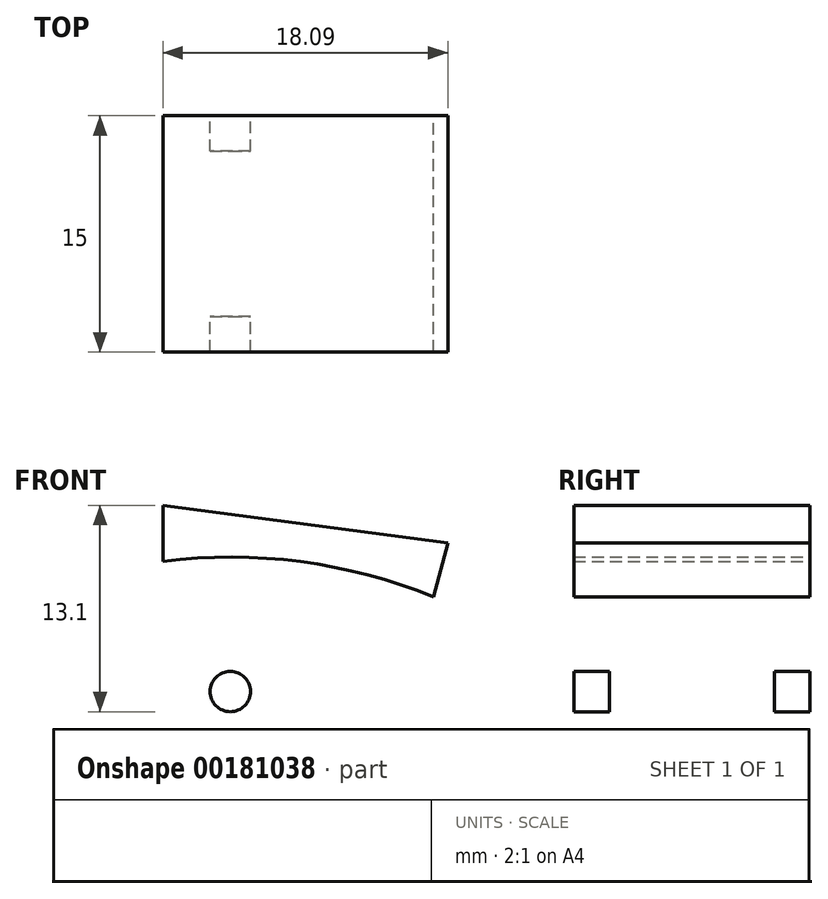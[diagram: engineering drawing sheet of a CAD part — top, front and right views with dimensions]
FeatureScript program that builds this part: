
annotation { "Feature Type Name" : "Feature", "Feature Type Description" : "" }
export const myFeature = defineFeature(function(context is Context, id is Id, definition is map)
    precondition{}
    {
        {
            var Q0;
            Q0=qCreatedBy(makeId("Front.planeOp"),FACE);
            var sketch = newSketch(context, id + "F0", { "sketchPlane" : qUnion([Q0])});
            skLineSegment(sketch, "E0", {"start": v(-9.28, 8.06) * mm, "end": v(8.83, 5.68) * mm});
            skCircle(sketch, "E1", {"center": v(-5, -3.76) * mm, "radius": 1.28 * mm});
            skCircle(sketch, "E2", {"center": v(1.63, -4.63) * mm, "radius": 1.28 * mm});
            skLineSegment(sketch, "E3", {"start": v(5.05, -8.35) * mm, "end": v(8.81, 5.68) * mm});
            skArc(sketch, "E4", {"start": v(-9.27, 9.62) * mm, "mid": v(-9.28, 9.52) * mm, "end": v(-9.28, 9.43) * mm});
            skLineSegment(sketch, "E5", {"start": v(-9.28, 8.06) * mm, "end": v(-9.28, -6.46) * mm});
            skArc(sketch, "E6", {"start": v(2.78, -9.5) * mm, "mid": v(-2.22, -8.21) * mm, "end": v(-7.38, -8.16) * mm});
            skArc(sketch, "E7", {"start": v(7.9, 2.26) * mm, "mid": v(-0.55, 4.5) * mm, "end": v(-9.28, 4.52) * mm});
            skArc(sketch, "E8", {"start": v(-9.28, -6.46) * mm, "mid": v(-8.7, -7.74) * mm, "end": v(-7.38, -8.16) * mm});
            skArc(sketch, "E9", {"start": v(2.78, -9.5) * mm, "mid": v(4.17, -9.43) * mm, "end": v(5.05, -8.35) * mm});
            skSolve(sketch);
        }
        {
            var Q0;
            Q0=makeQuery(id+"F0.imprint","IMPRINT",FACE,{"disambiguationData":[TD([[makeQuery(id+"F0.imprint","IMPRINT",EDGE,{"derivedFrom":sQuery(id+"F0.wireOp",EDGE,"E1")}),1.0]])]});
            var Q1;
            {var subQ4=sQuery(id+"F0.wireOp",EDGE,"E0");Q1=makeQuery(id+"F0.imprint","IMPRINT",FACE,{"disambiguationData":[TD([[makeQuery(id+"F0.imprint","IMPRINT",EDGE,{"derivedFrom":subQ4}),-1.0]])]});}
            extrude(context, id + "F1", {"entities" : qUnion([Q0, Q1]), "endBound" : BoundingType.SYMMETRIC, "depth" : 15 * mm});
        }
        {
            var Q0;
            Q0=makeQuery(id+"F0.imprint","IMPRINT",FACE,{"disambiguationData":[TD([[makeQuery(id+"F0.imprint","IMPRINT",EDGE,{"derivedFrom":sQuery(id+"F0.wireOp",EDGE,"E1")}),1.0]])]});
            var Q1;
            Q1=makeQuery(id+"F0.imprint","IMPRINT",FACE,{"disambiguationData":[TD([[makeQuery(id+"F0.imprint","IMPRINT",EDGE,{"derivedFrom":sQuery(id+"F0.wireOp",EDGE,"E1")}),-1.0]])]});
            var Q2;
            Q2=makeQuery(id+"F0.imprint","IMPRINT",FACE,{"disambiguationData":[TD([[makeQuery(id+"F0.imprint","IMPRINT",EDGE,{"derivedFrom":sQuery(id+"F0.wireOp",EDGE,"E2")}),-1.0]])]});
            extrude(context, id + "F2", {"entities" : qUnion([Q0, Q1, Q2]), "operationType" : NewBodyOperationType.REMOVE, "endBound" : BoundingType.SYMMETRIC, "depth" : 10.5 * mm});
        }
    });
